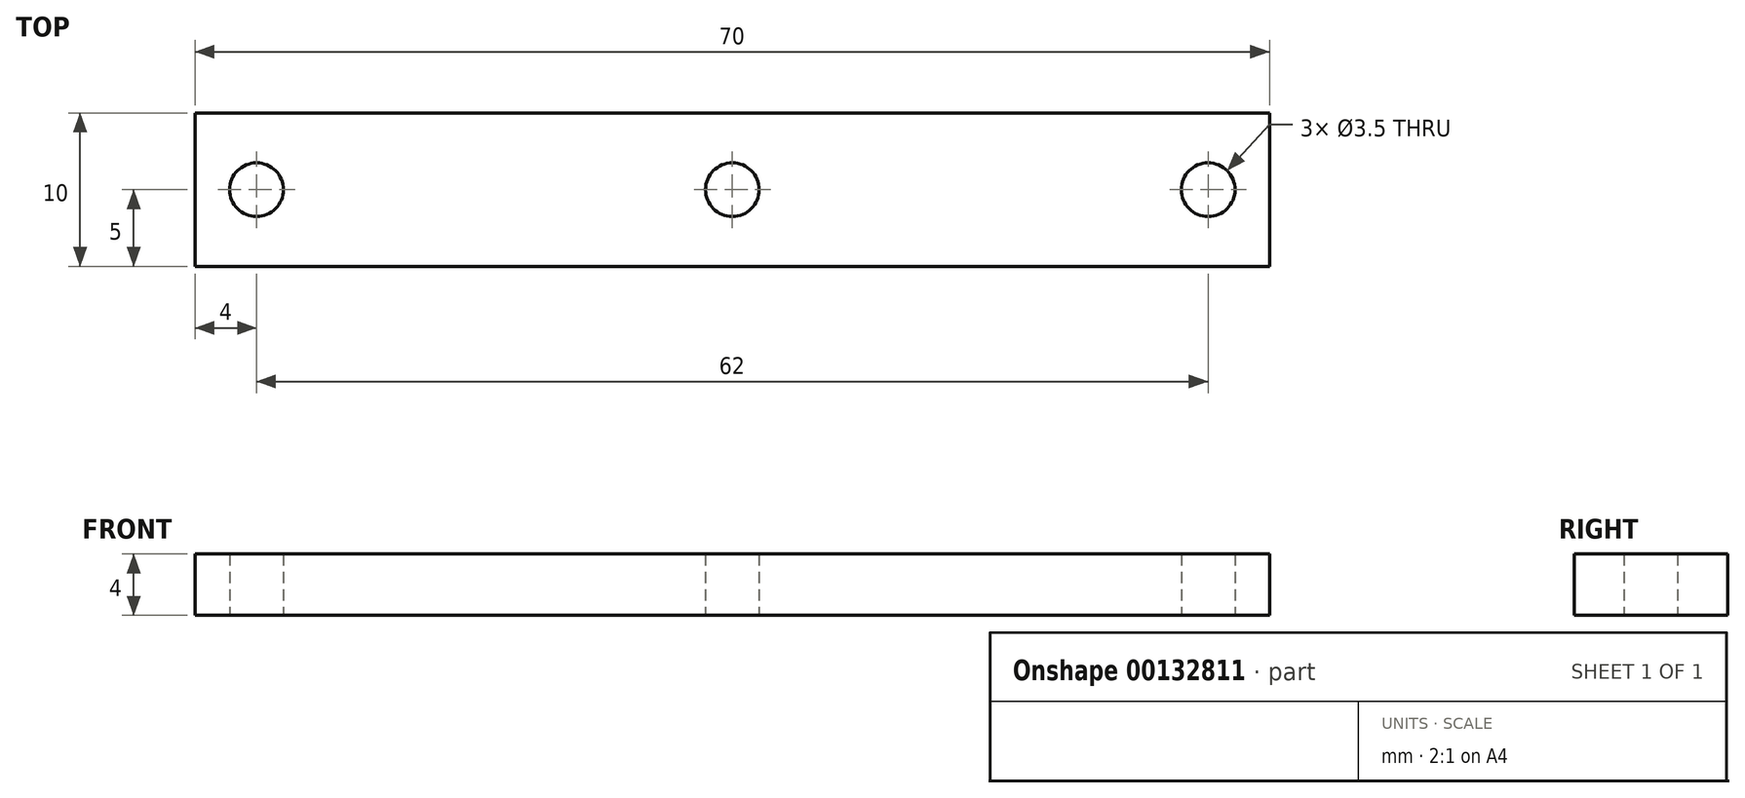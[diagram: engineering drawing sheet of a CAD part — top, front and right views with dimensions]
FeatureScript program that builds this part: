
annotation { "Feature Type Name" : "Feature", "Feature Type Description" : "" }
export const myFeature = defineFeature(function(context is Context, id is Id, definition is map)
    precondition{}
    {
        {
            var Q0;
            Q0=qCreatedBy(makeId("Top.planeOp"),FACE);
            var sketch = newSketch(context, id + "F0", { "sketchPlane" : qUnion([Q0])});
            skLineSegment(sketch, "E0.bottom", {"start": v(-4, 5) * mm, "end": v(66, 5) * mm});
            skLineSegment(sketch, "E0.top", {"start": v(-4, -5) * mm, "end": v(66, -5) * mm});
            skLineSegment(sketch, "E0.left", {"start": v(-4, 5) * mm, "end": v(-4, -5) * mm});
            skLineSegment(sketch, "E0.right", {"start": v(66, 5) * mm, "end": v(66, -5) * mm});
            skCircle(sketch, "E1", {"center": v(0, 0) * mm, "radius": 1.75 * mm});
            skCircle(sketch, "E2", {"center": v(31, 0) * mm, "radius": 1.75 * mm});
            skCircle(sketch, "E3", {"center": v(62, 0) * mm, "radius": 1.75 * mm});
            skSolve(sketch);
        }
        {
            var Q0;
            Q0=makeQuery(id+"F0.imprint","IMPRINT",FACE,{"disambiguationData":[TD([[makeQuery(id+"F0.imprint","IMPRINT",EDGE,{"derivedFrom":sQuery(id+"F0.wireOp",EDGE,"E0.bottom")}),-1.0]])]});
            extrude(context, id + "F1", {"entities" : qUnion([Q0]), "depth" : 4 * mm});
        }
    });
